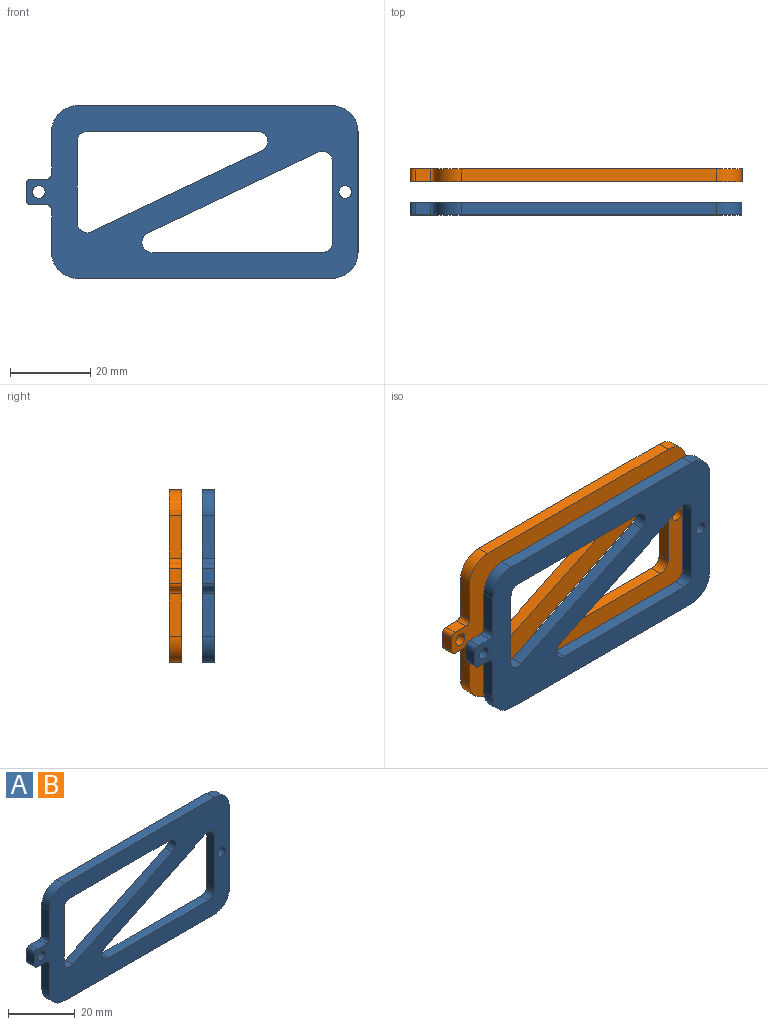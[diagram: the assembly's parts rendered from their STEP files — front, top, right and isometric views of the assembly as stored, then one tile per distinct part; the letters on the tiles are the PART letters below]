
ASSEMBLY  parts=2 mates=2
PART A: 32 faces, bbox 82.6x3.2x42.9 mm
  f0: plane 10.64x3.18mm, normal (-1,0,0), area 33.8mm2, adj f14,f15,f16,f27
  f1: plane 10.64x3.18mm, normal (-1,0,0), area 33.8mm2, adj f2,f15,f16,f28
  f2: cylinder r=6.35mm len=6.35mm, axis (0,1,0), area 31.7mm2, adj f1,f3,f15,f16
  f3: plane 63.5x3.18mm, normal (0,0,-1), area 201.6mm2, adj f2,f4,f15,f16
  f4: cylinder r=6.35mm len=6.35mm, axis (0,1,0), area 31.7mm2, adj f3,f5,f15,f16
  f5: plane 30.16x3.18mm, normal (1,0,0), area 95.8mm2, adj f4,f6,f15,f16
  f6: cylinder r=6.35mm len=6.35mm, axis (0,1,0), area 31.7mm2, adj f5,f7,f15,f16
  f7: plane 63.5x3.18mm, normal (0,0,1), area 201.6mm2, adj f6,f14,f15,f16
  f8: plane 42.29x20.09mm, normal (-0.43,0,0.9), area 148.7mm2, adj f15,f16,f20,f22
  f9: plane 20.09x3.18mm, normal (1,0,0), area 63.8mm2, adj f15,f16,f20,f21
  f10: plane 42.29x3.18mm, normal (0,0,1), area 134.3mm2, adj f15,f16,f17,f19
  f11: plane 42.29x20.09mm, normal (0.43,0,-0.9), area 148.7mm2, adj f15,f16,f17,f18
  f12: plane 42.29x3.18mm, normal (0,0,-1), area 134.3mm2, adj f15,f16,f21,f22
  f13: plane 20.09x3.18mm, normal (-1,0,0), area 63.8mm2, adj f15,f16,f18,f19
  f14: cylinder r=6.35mm len=6.35mm, axis (0,1,0), area 31.7mm2, adj f0,f7,f15,f16
  f15: plane 82.55x42.86mm, normal (0,-1,0), area 1811.1mm2, adj f0,f1,f2,f3,f4,f5,f6,f7
  f16: plane 82.55x42.86mm, normal (0,1,0), area 1811.1mm2, adj f0,f1,f2,f3,f4,f5,f6,f7
  f17: cylinder r=2.54mm len=4.83mm, axis (0,1,0), area 21.8mm2, adj f10,f11,f15,f16
  f18: cylinder r=2.54mm len=3.63mm, axis (0,-1,0), area 16.2mm2, adj f11,f13,f15,f16
  f19: cylinder r=2.54mm len=3.18mm, axis (0,1,0), area 12.7mm2, adj f10,f13,f15,f16
  f20: cylinder r=2.54mm len=3.63mm, axis (0,1,0), area 16.2mm2, adj f8,f9,f15,f16
  f21: cylinder r=2.54mm len=3.18mm, axis (0,1,0), area 12.7mm2, adj f9,f12,f15,f16
  f22: cylinder r=2.54mm len=4.83mm, axis (0,-1,0), area 21.8mm2, adj f8,f12,f15,f16
  f23: plane 3.81x3.18mm, normal (0,0,1), area 12.1mm2, adj f15,f16,f27,f29
  f24: plane 3.81x3.18mm, normal (0,0,-1), area 12.1mm2, adj f15,f16,f28,f30
  f25: plane 3.81x3.18mm, normal (-1,0,0), area 12.1mm2, adj f15,f16,f29,f30
  f26: cylinder r=1.59mm len=3.18mm, axis (0,1,0), area 31.7mm2, adj f15,f16
  f27: cylinder r=1.27mm len=3.18mm, axis (0,1,0), area 6.3mm2, adj f0,f15,f16,f23
  f28: cylinder r=1.27mm len=3.18mm, axis (0,-1,0), area 6.3mm2, adj f1,f15,f16,f24
  f29: cylinder r=1.27mm len=3.18mm, axis (0,1,0), area 6.3mm2, adj f15,f16,f23,f25
  f30: cylinder r=1.27mm len=3.18mm, axis (0,-1,0), area 6.3mm2, adj f15,f16,f24,f25
  f31: cylinder r=1.59mm len=3.18mm, axis (0,1,0), area 31.7mm2, adj f15,f16
PART B: same geometry as A
PLACE A rot(axis=(0,1,0),0deg) t=(-4.71,-7.6,5.43)mm
PLACE B t=(-4.71,0.66,5.43)mm fixed
MATE cylindrical B.f31 <-> A.f31  axis (0,1,0) through (30.21,-2.52,5.43)mm
MATE cylindrical A.f26 <-> B.f26  axis (0,1,0) through (-45.99,-9.18,5.43)mm
